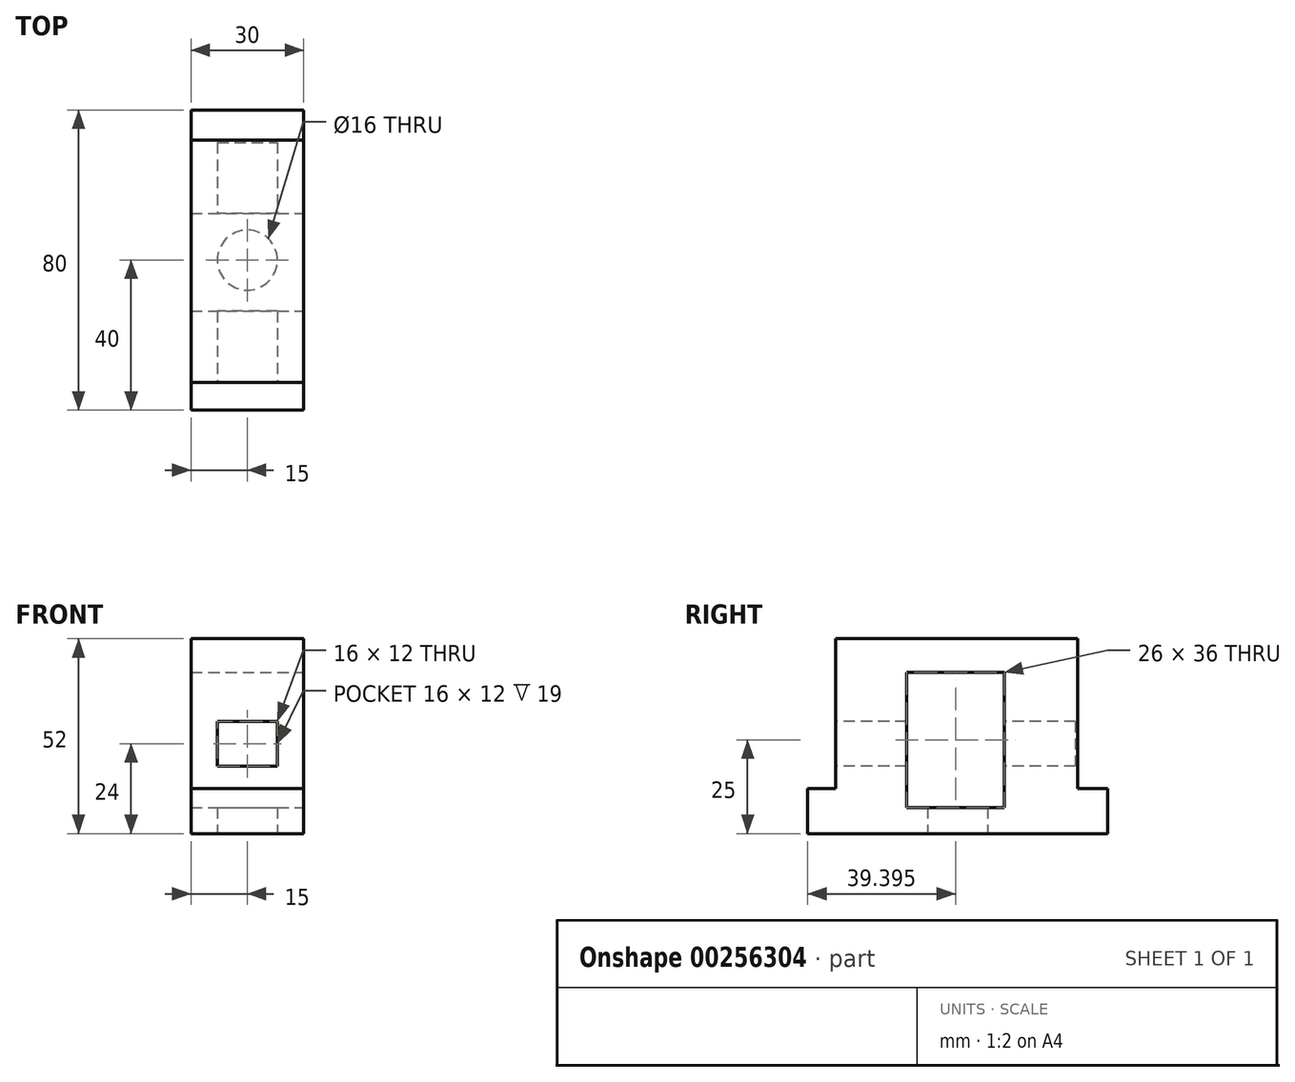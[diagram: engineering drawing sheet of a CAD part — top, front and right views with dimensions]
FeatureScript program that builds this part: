
annotation { "Feature Type Name" : "Feature", "Feature Type Description" : "" }
export const myFeature = defineFeature(function(context is Context, id is Id, definition is map)
    precondition{}
    {
        {
            var Q0;
            Q0=qCreatedBy(makeId("Top.planeOp"),FACE);
            var sketch = newSketch(context, id + "F0", { "sketchPlane" : qUnion([Q0])});
            skLineSegment(sketch, "E0.bottom", {"start": v(0, 0) * mm, "end": v(30, 0) * mm});
            skLineSegment(sketch, "E0.top", {"start": v(0, 80) * mm, "end": v(30, 80) * mm});
            skLineSegment(sketch, "E0.left", {"start": v(0, 0) * mm, "end": v(0, 80) * mm});
            skLineSegment(sketch, "E0.right", {"start": v(30, 0) * mm, "end": v(30, 80) * mm});
            skSolve(sketch);
        }
        {
            var Q0;
            Q0=makeQuery(id+"F0.imprint","IMPRINT",FACE,{"disambiguationData":[TD([[makeQuery(id+"F0.imprint","IMPRINT",EDGE,{"derivedFrom":sQuery(id+"F0.wireOp",EDGE,"E0.bottom")}),1.0]])]});
            extrude(context, id + "F1", {"entities" : qUnion([Q0]), "depth" : 52 * mm});
        }
        {
            var Q0;
            Q0=makeQuery(id+"F1.opExtrude","CAP_FACE",FACE,{"disambiguationData":[OSD([sQuery(id+"F0.wireOp",EDGE,"E0.bottom"),sQuery(id+"F0.wireOp",EDGE,"E0.top"),sQuery(id+"F0.wireOp",EDGE,"E0.left"),sQuery(id+"F0.wireOp",EDGE,"E0.right")])],"isStart":false});
            var sketch = newSketch(context, id + "F2", { "sketchPlane" : qUnion([Q0])});
            skLineSegment(sketch, "E1.bottom", {"start": v(0, 80) * mm, "end": v(30, 80) * mm});
            skLineSegment(sketch, "E1.top", {"start": v(0, 72) * mm, "end": v(30, 72) * mm});
            skLineSegment(sketch, "E1.left", {"start": v(0, 80) * mm, "end": v(0, 72) * mm});
            skLineSegment(sketch, "E1.right", {"start": v(30, 80) * mm, "end": v(30, 72) * mm});
            skLineSegment(sketch, "E2.bottom", {"start": v(0, 0) * mm, "end": v(30, 0) * mm});
            skLineSegment(sketch, "E2.top", {"start": v(0, 7.4) * mm, "end": v(30, 7.4) * mm});
            skLineSegment(sketch, "E2.left", {"start": v(0, 0) * mm, "end": v(0, 7.4) * mm});
            skLineSegment(sketch, "E2.right", {"start": v(30, 0) * mm, "end": v(30, 7.4) * mm});
            skSolve(sketch);
        }
        {
            var Q0;
            Q0=makeQuery(id+"F2.imprint","IMPRINT",FACE,{"disambiguationData":[TD([[makeQuery(id+"F2.imprint","IMPRINT",EDGE,{"derivedFrom":sQuery(id+"F2.wireOp",EDGE,"E1.bottom")}),-1.0]])]});
            var Q1;
            Q1=makeQuery(id+"F2.imprint","IMPRINT",FACE,{"disambiguationData":[TD([[makeQuery(id+"F2.imprint","IMPRINT",EDGE,{"derivedFrom":sQuery(id+"F2.wireOp",EDGE,"E2.bottom")}),1.0]])]});
            extrude(context, id + "F3", {"entities" : qUnion([Q0, Q1]), "operationType" : NewBodyOperationType.REMOVE, "oppositeDirection" : true, "depth" : 40 * mm});
        }
        {
            var Q0;
            Q0=makeQuery(id+"F3.boolean.opBoolean","COPY",FACE,{"derivedFrom":makeQuery(id+"F3.opExtrude","SWEPT_FACE",FACE,{"disambiguationData":[OSD([sQuery(id+"F2.wireOp",EDGE,"E2.top")])]})});
            var sketch = newSketch(context, id + "F4", { "sketchPlane" : qUnion([Q0])});
            skLineSegment(sketch, "E3.bottom", {"start": v(7, 30) * mm, "end": v(23, 30) * mm});
            skLineSegment(sketch, "E3.top", {"start": v(7, 18) * mm, "end": v(23, 18) * mm});
            skLineSegment(sketch, "E3.left", {"start": v(7, 30) * mm, "end": v(7, 18) * mm});
            skLineSegment(sketch, "E3.right", {"start": v(23, 30) * mm, "end": v(23, 18) * mm});
            skSolve(sketch);
        }
        {
            var Q0;
            Q0=makeQuery(id+"F4.imprint","IMPRINT",FACE,{"disambiguationData":[TD([[makeQuery(id+"F4.imprint","IMPRINT",EDGE,{"derivedFrom":sQuery(id+"F4.wireOp",EDGE,"E3.bottom")}),-1.0]])]});
            extrude(context, id + "F5", {"entities" : qUnion([Q0]), "operationType" : NewBodyOperationType.REMOVE, "oppositeDirection" : true, "depth" : 64 * mm});
        }
        {
            var Q0;
            Q0=makeQuery(id+"F1.opExtrude","SWEPT_FACE",FACE,{"disambiguationData":[OSD([sQuery(id+"F0.wireOp",EDGE,"E0.right")])]});
            var sketch = newSketch(context, id + "F6", { "sketchPlane" : qUnion([Q0])});
            skLineSegment(sketch, "E4.bottom", {"start": v(26.4, 43) * mm, "end": v(52.4, 43) * mm});
            skLineSegment(sketch, "E4.top", {"start": v(26.4, 7) * mm, "end": v(52.4, 7) * mm});
            skLineSegment(sketch, "E4.left", {"start": v(26.4, 43) * mm, "end": v(26.4, 7) * mm});
            skLineSegment(sketch, "E4.right", {"start": v(52.4, 43) * mm, "end": v(52.4, 7) * mm});
            skSolve(sketch);
        }
        {
            var Q0;
            Q0=makeQuery(id+"F6.imprint","IMPRINT",FACE,{"disambiguationData":[TD([[makeQuery(id+"F6.imprint","IMPRINT",EDGE,{"derivedFrom":sQuery(id+"F6.wireOp",EDGE,"E4.bottom")}),-1.0]])]});
            extrude(context, id + "F7", {"entities" : qUnion([Q0]), "operationType" : NewBodyOperationType.REMOVE, "oppositeDirection" : true, "depth" : 30 * mm});
        }
        {
            var Q0;
            Q0=makeQuery(id+"F1.opExtrude","CAP_FACE",FACE,{"disambiguationData":[OSD([sQuery(id+"F0.wireOp",EDGE,"E0.bottom"),sQuery(id+"F0.wireOp",EDGE,"E0.top"),sQuery(id+"F0.wireOp",EDGE,"E0.left"),sQuery(id+"F0.wireOp",EDGE,"E0.right")])],"isStart":true});
            var sketch = newSketch(context, id + "F8", { "sketchPlane" : qUnion([Q0])});
            skCircle(sketch, "E5", {"center": v(15, -40) * mm, "radius": 8 * mm});
            skPoint(sketch, "E5.centerSnap0", {"position": v(0, -40) * mm});
            skPoint(sketch, "E5.centerSnap1", {"position": v(15, 0) * mm});
            skSolve(sketch);
        }
        {
            var Q0;
            Q0=makeQuery(id+"F8.imprint","IMPRINT",FACE,{"disambiguationData":[TD([[makeQuery(id+"F8.imprint","IMPRINT",EDGE,{"derivedFrom":sQuery(id+"F8.wireOp",EDGE,"E5")}),1.0]])]});
            extrude(context, id + "F9", {"entities" : qUnion([Q0]), "operationType" : NewBodyOperationType.REMOVE, "oppositeDirection" : true, "depth" : 9 * mm});
        }
    });
